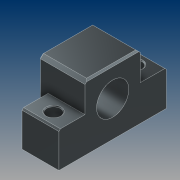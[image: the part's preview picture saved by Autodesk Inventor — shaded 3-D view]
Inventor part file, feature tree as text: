
AUTODESK INVENTOR PART (.ipt)
format: ipt  version: 2021 (Build 250183000, 183)  size: 205,824 bytes
history: native  units: mm
features: chamfer x6, sketch x4, projected_geometry x4, extrude x2, hole x2
ambient origin geometry x8: Origin, YZ Plane, XZ Plane, XY Plane, X Axis, Y Axis, Z Axis, Center Point
bodies: Solid1 (feature_tree)
feature tree (18):
  extrude  "Extrusion1"  Depth=70.0mm
  hole  "Hole1"  [1 undecoded]
  chamfer  "Chamfer1"  Distance=24.0mm
  chamfer  "Chamfer2"  Distance=1.0mm Angle=45.0deg
  chamfer  "Chamfer3"  Distance=1.0mm Angle=45.0deg
  extrude  "Extrusion2"  Depth=2.0mm TaperAngle=45.0deg
  hole  "Hole2"  [1 undecoded]
  chamfer  "Chamfer4"  Distance=5.5mm
  chamfer  "Chamfer5"  Distance=4.0mm
  chamfer  "Chamfer6"  Distance=2.0mm Angle=45.0deg
  sketch  "Sketch1"  dims[d0=36.0mm d1=70.0mm]
  sketch  "Sketch2"  dims[d2=19.0mm d3=24.0mm]
  projected_geometry  "Projected Loop1"
  projected_geometry  "Projected Loop2"
  sketch  "Sketch3"  dims[d4=21.0mm d5=24.0mm d6=0.0mm]
  projected_geometry  "Projected Loop3"
  sketch  "Sketch4"  dims[d7=9.0mm d8=6.0mm d9=4.0mm d10=2.0mm d11=90.0deg d12=8.0mm d13=20.594885mm d14=1.0mm d15=2.0mm d16=45.0deg d17=1.0mm d18=2.0mm d19=45.0deg d20=2.0mm d21=2.0mm d22=45.0deg d23=30.0mm d24=5.5mm d25=0.0mm d26=4.0mm d27=4.0mm d28=6.0mm d29=6.0mm d30=2.0mm d31=90.0deg d32=5.5mm d33=20.594885mm d34=2.0mm d35=2.0mm d36=45.0deg d37=0.5mm d38=2.0mm d39=45.0deg d40=0.5mm d41=2.0mm d42=45.0deg]
  projected_geometry  "Projected Loop4"
note: 2 required parameter values undecoded (feature->parameter linkage not recoverable at this tier; creation-order binding heuristic only, values carry confidence <= 0.55)
